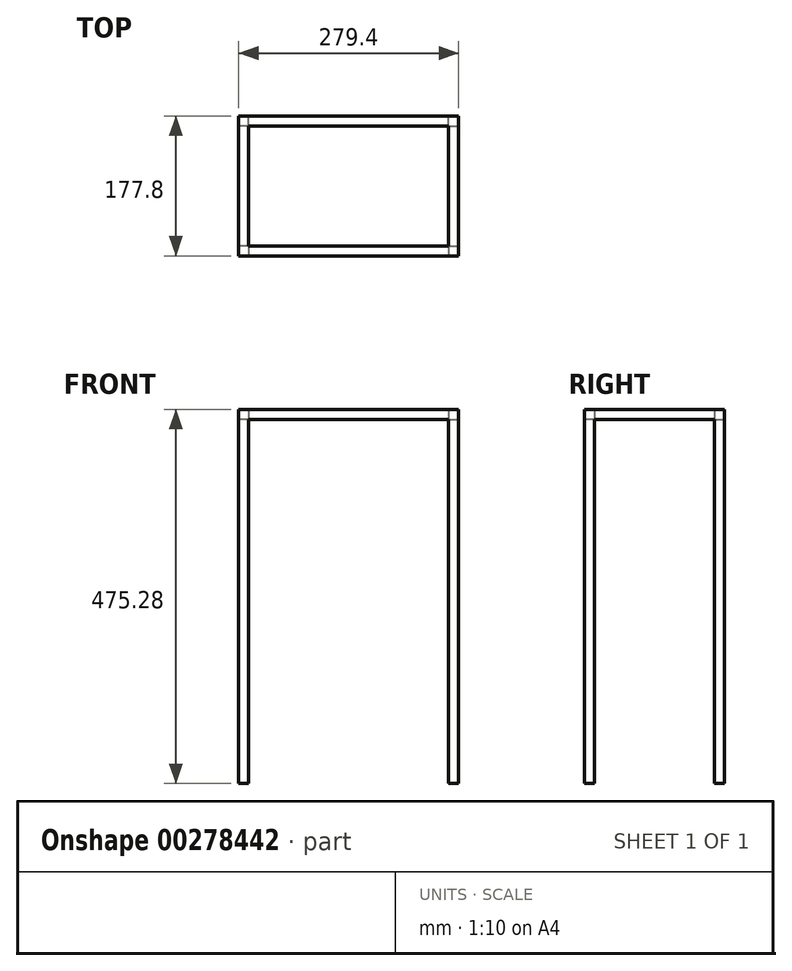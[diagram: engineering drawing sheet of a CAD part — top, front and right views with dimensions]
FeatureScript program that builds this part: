
annotation { "Feature Type Name" : "Feature", "Feature Type Description" : "" }
export const myFeature = defineFeature(function(context is Context, id is Id, definition is map)
    precondition{}
    {
        {
            var Q0;
            Q0=qCreatedBy(makeId("Top.planeOp"),FACE);
            var sketch = newSketch(context, id + "F0", { "sketchPlane" : qUnion([Q0])});
            skLineSegment(sketch, "E0.bottom", {"start": v(-127, -76.2) * mm, "end": v(127, -76.2) * mm});
            skLineSegment(sketch, "E0.top", {"start": v(-127, 76.2) * mm, "end": v(127, 76.2) * mm});
            skLineSegment(sketch, "E0.left", {"start": v(-127, -76.2) * mm, "end": v(-127, 76.2) * mm});
            skLineSegment(sketch, "E0.right", {"start": v(127, -76.2) * mm, "end": v(127, 76.2) * mm});
            skLineSegment(sketch, "E1.0", {"start": v(139.7, -88.9) * mm, "end": v(139.7, 88.9) * mm});
            skLineSegment(sketch, "E1.1", {"start": v(-139.7, -88.9) * mm, "end": v(139.7, -88.9) * mm});
            skLineSegment(sketch, "E1.2", {"start": v(-139.7, -88.9) * mm, "end": v(-139.7, 88.9) * mm});
            skLineSegment(sketch, "E1.3", {"start": v(-139.7, 88.9) * mm, "end": v(139.7, 88.9) * mm});
            skSolve(sketch);
        }
        {
            var Q0;
            Q0=makeQuery(id+"F0.imprint","IMPRINT",FACE,{"disambiguationData":[TD([[makeQuery(id+"F0.imprint","IMPRINT",EDGE,{"derivedFrom":sQuery(id+"F0.wireOp",EDGE,"E0.bottom")}),-1.0]])]});
            extrude(context, id + "F1", {"entities" : qUnion([Q0]), "depth" : 12.7 * mm});
        }
        {
            var Q0;
            Q0=makeQuery(id+"F1.opExtrude","CAP_FACE",FACE,{"disambiguationData":[OSD([sQuery(id+"F0.wireOp",EDGE,"E0.bottom"),sQuery(id+"F0.wireOp",EDGE,"E0.top"),sQuery(id+"F0.wireOp",EDGE,"E0.left"),sQuery(id+"F0.wireOp",EDGE,"E0.right"),sQuery(id+"F0.wireOp",EDGE,"E1.0"),sQuery(id+"F0.wireOp",EDGE,"E1.1"),sQuery(id+"F0.wireOp",EDGE,"E1.2"),sQuery(id+"F0.wireOp",EDGE,"E1.3")])],"isStart":false});
            var sketch = newSketch(context, id + "F2", { "sketchPlane" : qUnion([Q0])});
            skLineSegment(sketch, "E2.0", {"start": v(127, -76.2) * mm, "end": v(127, 76.2) * mm});
            skLineSegment(sketch, "E3.0", {"start": v(139.7, -88.9) * mm, "end": v(139.7, 88.9) * mm});
            skLineSegment(sketch, "E4.0", {"start": v(-139.7, -88.9) * mm, "end": v(139.7, -88.9) * mm});
            skLineSegment(sketch, "E5.0", {"start": v(-127, -76.2) * mm, "end": v(127, -76.2) * mm});
            skLineSegment(sketch, "E6.0", {"start": v(-127, 76.2) * mm, "end": v(127, 76.2) * mm});
            skLineSegment(sketch, "E7.0", {"start": v(-139.7, 88.9) * mm, "end": v(139.7, 88.9) * mm});
            skLineSegment(sketch, "E8.0", {"start": v(-139.7, -88.9) * mm, "end": v(-139.7, 88.9) * mm});
            skLineSegment(sketch, "E9.0", {"start": v(-127, -76.2) * mm, "end": v(-127, 76.2) * mm});
            skLineSegment(sketch, "E10", {"start": v(127, -76.2) * mm, "end": v(139.7, -76.2) * mm});
            skLineSegment(sketch, "E11", {"start": v(139.7, -76.2) * mm, "end": v(139.7, -76.2) * mm});
            skLineSegment(sketch, "E12", {"start": v(127, -76.2) * mm, "end": v(127, -88.9) * mm});
            skLineSegment(sketch, "E13", {"start": v(127, 76.2) * mm, "end": v(139.7, 76.2) * mm});
            skLineSegment(sketch, "E14", {"start": v(127, 76.2) * mm, "end": v(127, 88.9) * mm});
            skLineSegment(sketch, "E15", {"start": v(-127, 76.2) * mm, "end": v(-127, 88.9) * mm});
            skLineSegment(sketch, "E16", {"start": v(-127, 76.2) * mm, "end": v(-139.7, 76.2) * mm});
            skLineSegment(sketch, "E17", {"start": v(-127, -76.2) * mm, "end": v(-127, -88.9) * mm});
            skLineSegment(sketch, "E18", {"start": v(-127, -76.2) * mm, "end": v(-139.7, -76.2) * mm});
            skSolve(sketch);
        }
        {
            var Q0;
            {var subQ3=sQuery(id+"F2.wireOp",EDGE,"E17");Q0=makeQuery(id+"F2.imprint","IMPRINT",FACE,{"disambiguationData":[TD([[makeQuery(id+"F2.imprint","IMPRINT",EDGE,{"derivedFrom":subQ3}),-1.0]])]});}
            var Q1;
            {var subQ3=sQuery(id+"F2.wireOp",EDGE,"E15");Q1=makeQuery(id+"F2.imprint","IMPRINT",FACE,{"disambiguationData":[TD([[makeQuery(id+"F2.imprint","IMPRINT",EDGE,{"derivedFrom":subQ3}),1.0]])]});}
            var Q2;
            {var subQ3=sQuery(id+"F2.wireOp",EDGE,"E10");Q2=makeQuery(id+"F2.imprint","IMPRINT",FACE,{"disambiguationData":[TD([[makeQuery(id+"F2.imprint","IMPRINT",EDGE,{"derivedFrom":subQ3}),-1.0]])]});}
            var Q3;
            {var subQ3=sQuery(id+"F2.wireOp",EDGE,"E13");Q3=makeQuery(id+"F2.imprint","IMPRINT",FACE,{"disambiguationData":[TD([[makeQuery(id+"F2.imprint","IMPRINT",EDGE,{"derivedFrom":subQ3}),1.0]])]});}
            extrude(context, id + "F3", {"entities" : qUnion([Q0, Q1, Q2, Q3]), "operationType" : NewBodyOperationType.ADD, "oppositeDirection" : true, "depth" : 475.28 * mm});
        }
    });
